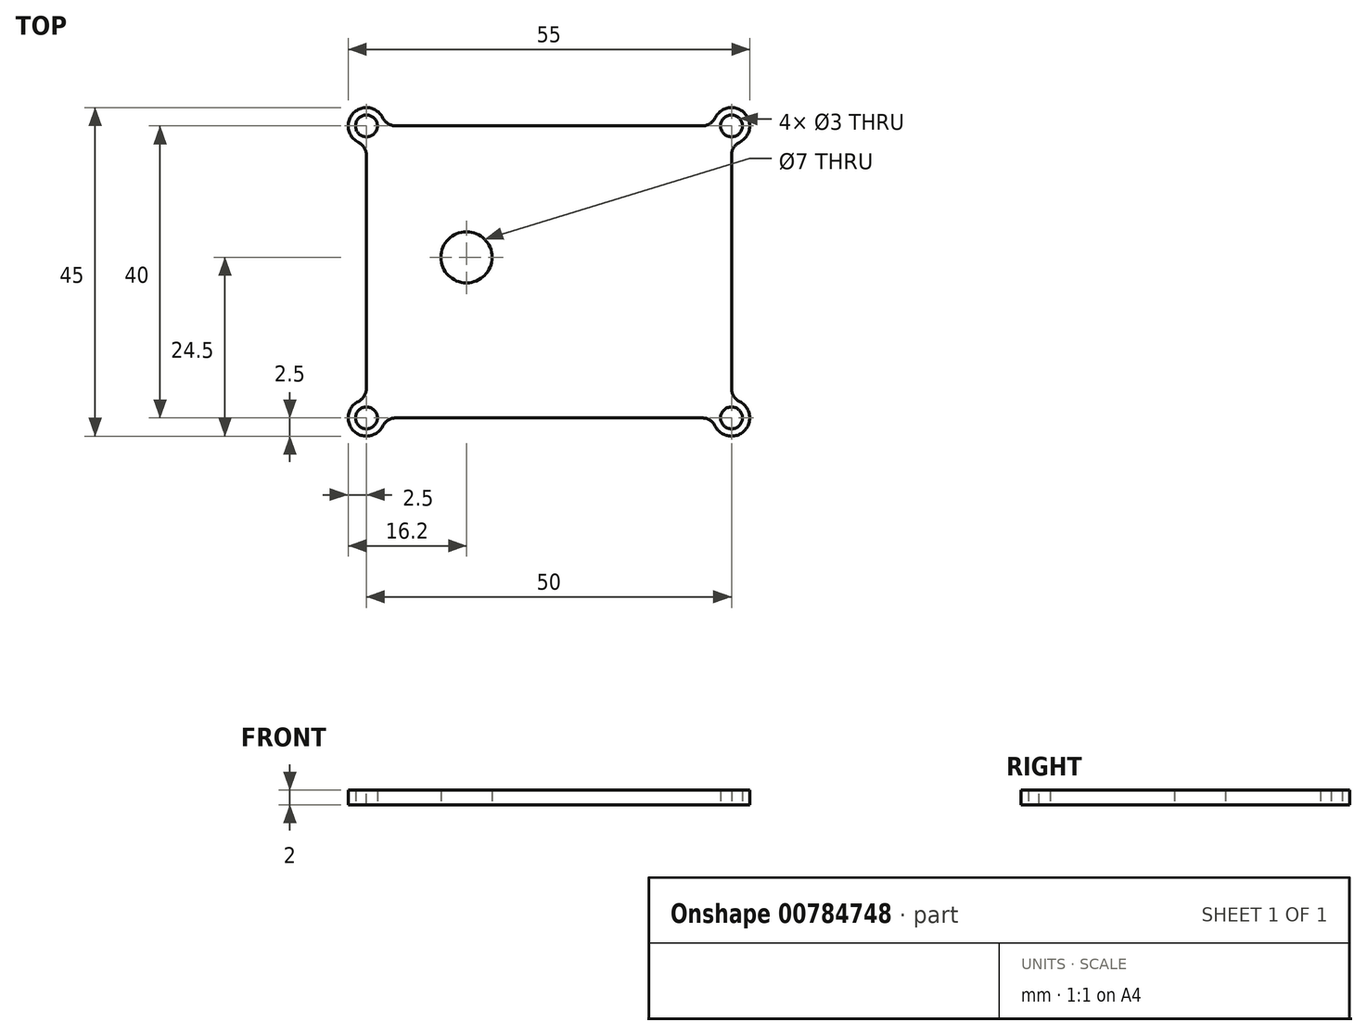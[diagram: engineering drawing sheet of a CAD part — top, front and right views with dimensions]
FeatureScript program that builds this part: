
annotation { "Feature Type Name" : "Feature", "Feature Type Description" : "" }
export const myFeature = defineFeature(function(context is Context, id is Id, definition is map)
    precondition{}
    {
        {
            var Q0;
            Q0=qCreatedBy(makeId("Top.planeOp"),FACE);
            var sketch = newSketch(context, id + "F0", { "sketchPlane" : qUnion([Q0])});
            skLineSegment(sketch, "E0.bottom", {"start": v(-25, 20) * mm, "end": v(25, 20) * mm});
            skLineSegment(sketch, "E0.top", {"start": v(-25, -20) * mm, "end": v(25, -20) * mm});
            skLineSegment(sketch, "E0.left", {"start": v(-25, 20) * mm, "end": v(-25, -20) * mm});
            skLineSegment(sketch, "E0.right", {"start": v(25, 20) * mm, "end": v(25, -20) * mm});
            skCircle(sketch, "E1", {"center": v(25, 20) * mm, "radius": 2.5 * mm});
            skCircle(sketch, "E2", {"center": v(-25, 20) * mm, "radius": 2.5 * mm});
            skCircle(sketch, "E3", {"center": v(-25, -20) * mm, "radius": 2.5 * mm});
            skCircle(sketch, "E4", {"center": v(25, -20) * mm, "radius": 2.5 * mm});
            skLineSegment(sketch, "E5.bottom", {"start": v(-19.8, 14.3) * mm, "end": v(19.8, 14.3) * mm, "construction": true});
            skLineSegment(sketch, "E5.top", {"start": v(-19.8, -14.3) * mm, "end": v(19.8, -14.3) * mm, "construction": true});
            skLineSegment(sketch, "E5.left", {"start": v(-19.8, 14.3) * mm, "end": v(-19.8, -14.3) * mm, "construction": true});
            skLineSegment(sketch, "E5.right", {"start": v(19.8, 14.3) * mm, "end": v(19.8, -14.3) * mm, "construction": true});
            skPoint(sketch, "E6", {"position": v(-19.8, 14.3) * mm});
            skPoint(sketch, "E7", {"position": v(19.8, 14.3) * mm});
            skPoint(sketch, "E8", {"position": v(19.8, -14.3) * mm});
            skPoint(sketch, "E9", {"position": v(-19.8, -14.3) * mm});
            skCircle(sketch, "E10", {"center": v(-11.3, 2) * mm, "radius": 3.5 * mm});
            skSolve(sketch);
        }
        {
            var Q0;
            Q0 = qSketchRegion(id + "F0", true);
            extrude(context, id + "F1", {"entities" : qUnion([Q0]), "depth" : 2 * mm, "offsetDistance" : 25 * mm});
        }
        {
            var Q0;
            Q0=makeQuery(id+"F1.opExtrude","CAP_FACE",FACE,{"disambiguationData":[OSD([sQuery(id+"F0.wireOp",EDGE,"E0.bottom"),sQuery(id+"F0.wireOp",EDGE,"E0.top"),sQuery(id+"F0.wireOp",EDGE,"E0.left"),sQuery(id+"F0.wireOp",EDGE,"E0.right"),sQuery(id+"F0.wireOp",EDGE,"E1"),sQuery(id+"F0.wireOp",EDGE,"E2"),sQuery(id+"F0.wireOp",EDGE,"E3"),sQuery(id+"F0.wireOp",EDGE,"E4"),sQuery(id+"F0.wireOp",EDGE,"E10")])],"isStart":false});
            var sketch = newSketch(context, id + "F2", { "sketchPlane" : qUnion([Q0])});
            skPoint(sketch, "E11", {"position": v(-25, 20) * mm});
            skPoint(sketch, "E12", {"position": v(25, 20) * mm});
            skPoint(sketch, "E13", {"position": v(25, -20) * mm});
            skPoint(sketch, "E14", {"position": v(-25, -20) * mm});
            skSolve(sketch);
        }
        {
            var Q0;
            Q0=sQuery(id+"F2.wireOp",VERTEX,"E11");
            var Q1;
            Q1=sQuery(id+"F2.wireOp",VERTEX,"E14");
            var Q2;
            Q2=sQuery(id+"F2.wireOp",VERTEX,"E12");
            var Q3;
            Q3=sQuery(id+"F2.wireOp",VERTEX,"E13");
            var Q4;
            Q4=makeQuery(id+"F1.opExtrude","SWEPT_BODY",BODY,{"disambiguationData":[OSD([sQuery(id+"F0.wireOp",EDGE,"E0.bottom"),sQuery(id+"F0.wireOp",EDGE,"E0.top"),sQuery(id+"F0.wireOp",EDGE,"E0.left"),sQuery(id+"F0.wireOp",EDGE,"E0.right"),sQuery(id+"F0.wireOp",EDGE,"E1"),sQuery(id+"F0.wireOp",EDGE,"E2"),sQuery(id+"F0.wireOp",EDGE,"E3"),sQuery(id+"F0.wireOp",EDGE,"E4"),sQuery(id+"F0.wireOp",EDGE,"E10")])]});
            hole(context, id + "F3", {"style" : HoleStyle.SIMPLE, "endStyle" : HoleEndStyle.THROUGH, "holeDiameter" : 3 * mm, "majorDiameter" : 5 * mm, "isTappedThrough" : true, "tappedDepth" : 12 * mm, "tapClearance" : 3, "locations" : qUnion([Q0, Q1, Q2, Q3]), "scope" : qUnion([Q4]), "startStyle" : HoleStartStyle.SKETCH});
        }
        {
            var Q0;
            Q0=makeQuery(id+"F1.opExtrude","SWEPT_EDGE",EDGE,{"disambiguationData":[OSD([sQuery(id+"F0.wireOp",EDGE,"E0.left"),sQuery(id+"F0.wireOp",EDGE,"E2")])]});
            var Q1;
            Q1=makeQuery(id+"F1.opExtrude","SWEPT_EDGE",EDGE,{"disambiguationData":[OSD([sQuery(id+"F0.wireOp",EDGE,"E0.bottom"),sQuery(id+"F0.wireOp",EDGE,"E2")])]});
            var Q2;
            Q2=makeQuery(id+"F1.opExtrude","SWEPT_EDGE",EDGE,{"disambiguationData":[OSD([sQuery(id+"F0.wireOp",EDGE,"E0.bottom"),sQuery(id+"F0.wireOp",EDGE,"E1")])]});
            var Q3;
            Q3=makeQuery(id+"F1.opExtrude","SWEPT_EDGE",EDGE,{"disambiguationData":[OSD([sQuery(id+"F0.wireOp",EDGE,"E0.right"),sQuery(id+"F0.wireOp",EDGE,"E1")])]});
            var Q4;
            Q4=makeQuery(id+"F1.opExtrude","SWEPT_EDGE",EDGE,{"disambiguationData":[OSD([sQuery(id+"F0.wireOp",EDGE,"E0.right"),sQuery(id+"F0.wireOp",EDGE,"E4")])]});
            var Q5;
            Q5=makeQuery(id+"F1.opExtrude","SWEPT_EDGE",EDGE,{"disambiguationData":[OSD([sQuery(id+"F0.wireOp",EDGE,"E0.top"),sQuery(id+"F0.wireOp",EDGE,"E4")])]});
            var Q6;
            Q6=makeQuery(id+"F1.opExtrude","SWEPT_EDGE",EDGE,{"disambiguationData":[OSD([sQuery(id+"F0.wireOp",EDGE,"E0.top"),sQuery(id+"F0.wireOp",EDGE,"E3")])]});
            var Q7;
            Q7=makeQuery(id+"F1.opExtrude","SWEPT_EDGE",EDGE,{"disambiguationData":[OSD([sQuery(id+"F0.wireOp",EDGE,"E0.left"),sQuery(id+"F0.wireOp",EDGE,"E3")])]});
            fillet(context, id + "F4", {"entities" : qUnion([Q0, Q1, Q2, Q3, Q4, Q5, Q6, Q7]), "radius" : 2 * mm, "tangentPropagation" : true, "allowEdgeOverflow" : false});
        }
    });
